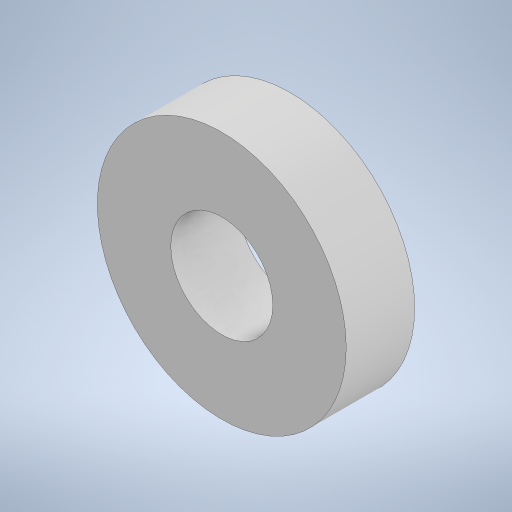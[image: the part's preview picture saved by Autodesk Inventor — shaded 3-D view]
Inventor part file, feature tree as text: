
AUTODESK INVENTOR PART (.ipt)
format: ipt  version: 2024.3 (Build 283343000, 343)  size: 216,064 bytes
history: native  units: mm
features: other x1, extrude x1, sketch x1
ambient origin geometry x8: Origin, YZ Plane, XZ Plane, XY Plane, X Axis, Y Axis, Z Axis, Center Point
bodies: Body1 (feature_tree)
feature tree (3):
  other  "ソリッド1"
  extrude  "押し出し1"  Depth=8.2mm
  sketch  "スケッチ1"
